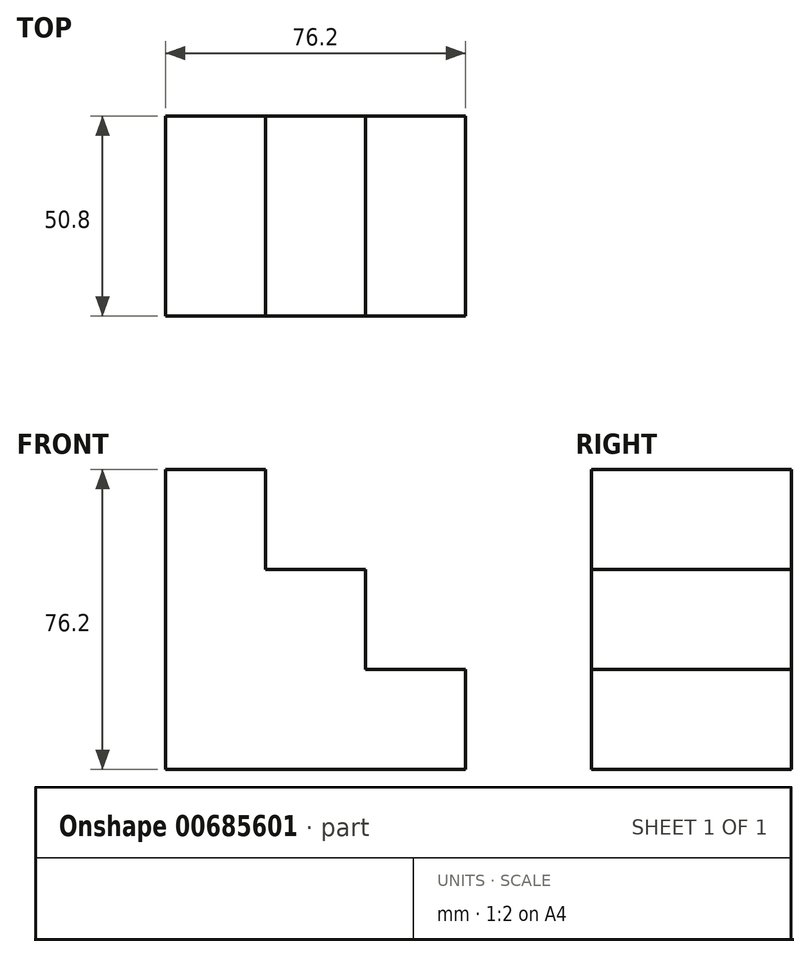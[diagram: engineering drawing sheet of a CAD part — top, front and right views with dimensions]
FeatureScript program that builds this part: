
annotation { "Feature Type Name" : "Feature", "Feature Type Description" : "" }
export const myFeature = defineFeature(function(context is Context, id is Id, definition is map)
    precondition{}
    {
        {
            var Q0;
            Q0=qCreatedBy(makeId("Front.planeOp"),FACE);
            var sketch = newSketch(context, id + "F0", { "sketchPlane" : qUnion([Q0])});
            skLineSegment(sketch, "E0", {"start": v(0, 76.2) * mm, "end": v(0, 0) * mm});
            skLineSegment(sketch, "E1", {"start": v(0, 0) * mm, "end": v(76.2, 0) * mm});
            skLineSegment(sketch, "E2", {"start": v(0, 76.2) * mm, "end": v(25.4, 76.2) * mm});
            skLineSegment(sketch, "E3", {"start": v(25.4, 76.2) * mm, "end": v(25.4, 50.8) * mm});
            skLineSegment(sketch, "E4", {"start": v(25.4, 50.8) * mm, "end": v(50.8, 50.8) * mm});
            skLineSegment(sketch, "E5", {"start": v(50.8, 50.8) * mm, "end": v(50.8, 25.4) * mm});
            skLineSegment(sketch, "E6", {"start": v(50.8, 25.4) * mm, "end": v(76.2, 25.4) * mm});
            skLineSegment(sketch, "E7", {"start": v(76.2, 25.4) * mm, "end": v(76.2, 0) * mm});
            skSolve(sketch);
        }
        {
            var Q0;
            Q0 = qSketchRegion(id + "F0", true);
            extrude(context, id + "F1", {"entities" : qUnion([Q0]), "depth" : 50.8 * mm, "offsetDistance" : 25.4 * mm});
        }
    });
